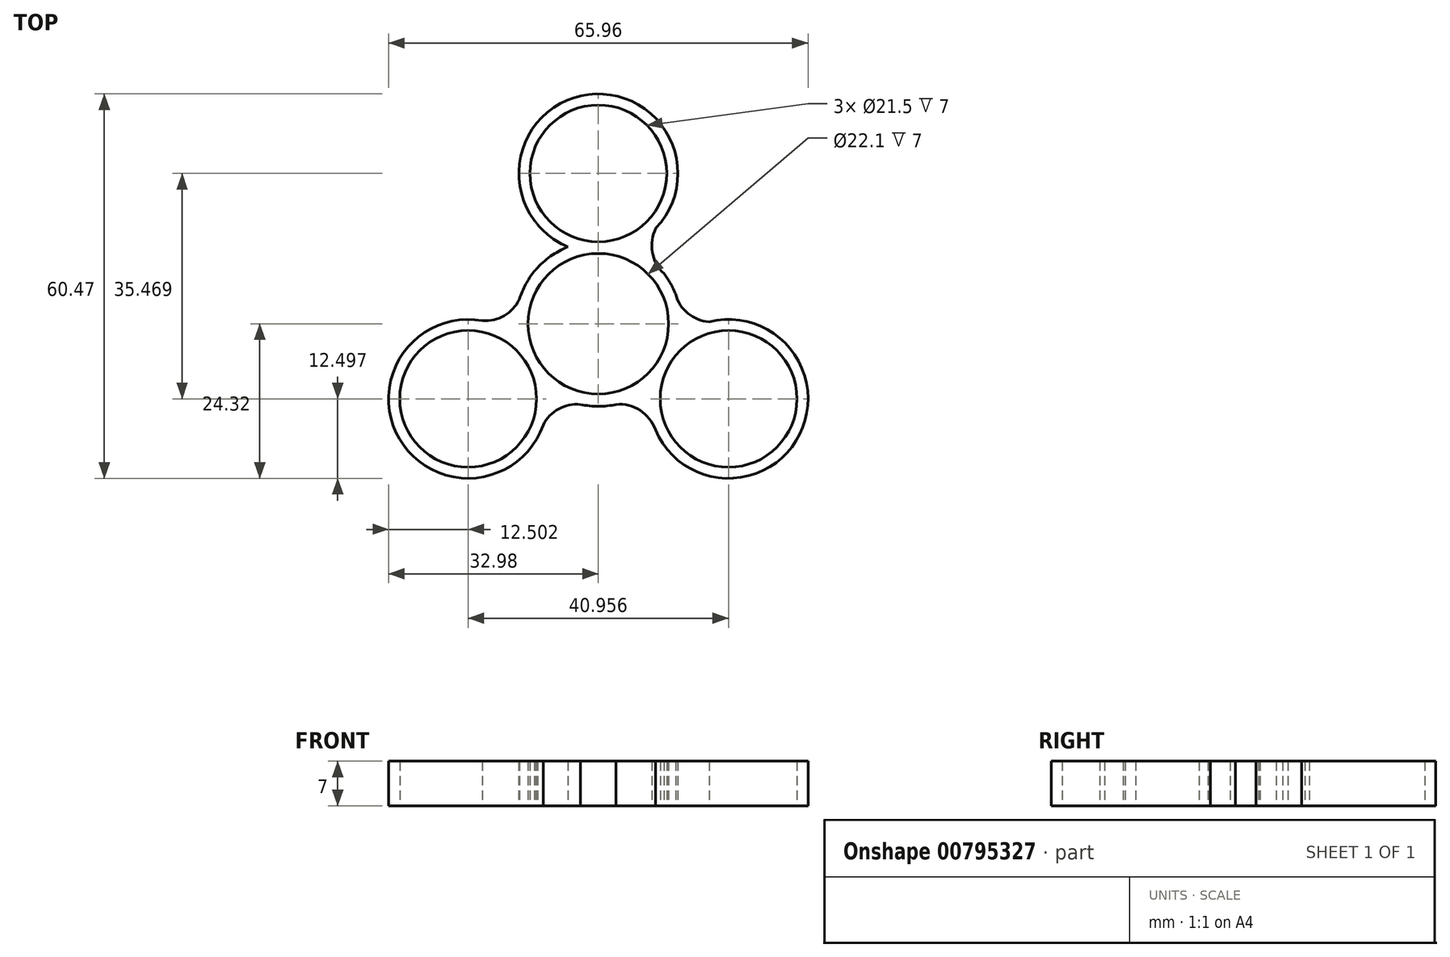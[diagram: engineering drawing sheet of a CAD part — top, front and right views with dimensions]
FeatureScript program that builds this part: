
annotation { "Feature Type Name" : "Feature", "Feature Type Description" : "" }
export const myFeature = defineFeature(function(context is Context, id is Id, definition is map)
    precondition{}
    {
        {
            var Q0;
            Q0=qCreatedBy(makeId("Top.planeOp"),FACE);
            var sketch = newSketch(context, id + "F0", { "sketchPlane" : qUnion([Q0])});
            skCircle(sketch, "E0", {"center": v(0, 0) * mm, "radius": 11.05 * mm});
            skCircle(sketch, "E1", {"center": v(0, 0) * mm, "radius": 13 * mm});
            skCircle(sketch, "E2", {"center": v(0, 23.65) * mm, "radius": 10.75 * mm});
            skCircle(sketch, "E3", {"center": v(0, 23.65) * mm, "radius": 12.5 * mm});
            skCircle(sketch, "E4", {"center": v(20.48, -11.82) * mm, "radius": 10.75 * mm});
            skCircle(sketch, "E5", {"center": v(20.48, -11.82) * mm, "radius": 12.5 * mm});
            skCircle(sketch, "E6", {"center": v(-20.48, -11.82) * mm, "radius": 10.75 * mm});
            skCircle(sketch, "E7", {"center": v(-20.48, -11.82) * mm, "radius": 12.5 * mm});
            skArc(sketch, "E8", {"start": v(-10.03, 8.27) * mm, "mid": v(-8.52, 12.26) * mm, "end": v(-10.07, 16.24) * mm});
            skArc(sketch, "E9", {"start": v(-19, 0.58) * mm, "mid": v(-14.79, 1.27) * mm, "end": v(-12.12, 4.6) * mm});
            skArc(sketch, "E10", {"start": v(9.9, 16.23) * mm, "mid": v(8.4, 11.97) * mm, "end": v(10.33, 7.9) * mm});
            skArc(sketch, "E11", {"start": v(12.14, 4.65) * mm, "mid": v(14.59, 1.27) * mm, "end": v(18.66, 0.33) * mm});
            skArc(sketch, "E12", {"start": v(9, -16.77) * mm, "mid": v(6.3, -13.46) * mm, "end": v(2.07, -12.8) * mm});
            skArc(sketch, "E13", {"start": v(-2.15, -12.8) * mm, "mid": v(-6.38, -13.49) * mm, "end": v(-9.04, -16.85) * mm});
            skSolve(sketch);
        }
        {
            var Q0;
            {var subQ1=sQuery(id+"F0.wireOp",EDGE,"E1");var subQ4=sQuery(id+"F0.wireOp",EDGE,"E7");var subQ7=makeQuery(id+"F0.imprint","INTERSECT",VERTEX,{"disambiguationData":[OD(0.0)],"derivedFrom":[subQ1,subQ4]});Q0=makeQuery(id+"F0.imprint","IMPRINT",FACE,{"disambiguationData":[TD([[makeQuery(id+"F0.imprint","IMPRINT",EDGE,{"disambiguationData":[TD([[subQ7,-1.0]])],"derivedFrom":subQ1}),-1.0]])]});}
            var Q1;
            {var subQ0=sQuery(id+"F0.wireOp",EDGE,"E9");var subQ1=sQuery(id+"F0.wireOp",EDGE,"E1");var subQ2=makeQuery(id+"F0.imprint","INTERSECT",VERTEX,{"derivedFrom":[subQ1,subQ0]});Q1=makeQuery(id+"F0.imprint","IMPRINT",FACE,{"disambiguationData":[TD([[makeQuery(id+"F0.imprint","IMPRINT",EDGE,{"disambiguationData":[TD([[subQ2,-1.0]])],"derivedFrom":subQ1}),-1.0]])]});}
            var Q2;
            Q2=makeQuery(id+"F0.imprint","IMPRINT",FACE,{"disambiguationData":[TD([[makeQuery(id+"F0.imprint","IMPRINT",EDGE,{"derivedFrom":sQuery(id+"F0.wireOp",EDGE,"E0")}),-1.0]])]});
            var Q3;
            {var subQ0=sQuery(id+"F0.wireOp",EDGE,"E7");var subQ1=sQuery(id+"F0.wireOp",EDGE,"E1");var subQ2=makeQuery(id+"F0.imprint","INTERSECT",VERTEX,{"disambiguationData":[OD(0.0)],"derivedFrom":[subQ1,subQ0]});Q3=makeQuery(id+"F0.imprint","IMPRINT",FACE,{"disambiguationData":[TD([[makeQuery(id+"F0.imprint","IMPRINT",EDGE,{"disambiguationData":[TD([[subQ2,-1.0]])],"derivedFrom":subQ1}),1.0]])]});}
            var Q4;
            {var subQ0=sQuery(id+"F0.wireOp",EDGE,"E12");var subQ1=sQuery(id+"F0.wireOp",EDGE,"E5");var subQ2=makeQuery(id+"F0.imprint","INTERSECT",VERTEX,{"disambiguationData":[OD(1.0)],"derivedFrom":[subQ1,subQ0]});Q4=makeQuery(id+"F0.imprint","IMPRINT",FACE,{"disambiguationData":[TD([[makeQuery(id+"F0.imprint","IMPRINT",EDGE,{"disambiguationData":[TD([[subQ2,1.0]])],"derivedFrom":subQ1}),-1.0]])]});}
            var Q5;
            {var subQ0=sQuery(id+"F0.wireOp",EDGE,"E13");var subQ1=sQuery(id+"F0.wireOp",EDGE,"E1");var subQ2=makeQuery(id+"F0.imprint","INTERSECT",VERTEX,{"derivedFrom":[subQ1,subQ0]});Q5=makeQuery(id+"F0.imprint","IMPRINT",FACE,{"disambiguationData":[TD([[makeQuery(id+"F0.imprint","IMPRINT",EDGE,{"disambiguationData":[TD([[subQ2,1.0]])],"derivedFrom":subQ1}),-1.0]])]});}
            var Q6;
            {var subQ3=sQuery(id+"F0.wireOp",EDGE,"E1");var subQ8=sQuery(id+"F0.wireOp",EDGE,"E4");var subQ9=makeQuery(id+"F0.imprint","INTERSECT",VERTEX,{"disambiguationData":[OD(0.0)],"derivedFrom":[subQ8,subQ3]});Q6=makeQuery(id+"F0.imprint","IMPRINT",FACE,{"disambiguationData":[TD([[makeQuery(id+"F0.imprint","IMPRINT",EDGE,{"disambiguationData":[TD([[subQ9,-1.0]])],"derivedFrom":subQ8}),-1.0]])]});}
            var Q7;
            {var subQ0=sQuery(id+"F0.wireOp",EDGE,"E1");var subQ1=sQuery(id+"F0.wireOp",EDGE,"E4");var subQ2=makeQuery(id+"F0.imprint","INTERSECT",VERTEX,{"disambiguationData":[OD(0.0)],"derivedFrom":[subQ1,subQ0]});Q7=makeQuery(id+"F0.imprint","IMPRINT",FACE,{"disambiguationData":[TD([[makeQuery(id+"F0.imprint","IMPRINT",EDGE,{"disambiguationData":[TD([[subQ2,1.0]])],"derivedFrom":subQ1}),-1.0]])]});}
            var Q8;
            {var subQ0=sQuery(id+"F0.wireOp",EDGE,"E11");var subQ1=sQuery(id+"F0.wireOp",EDGE,"E5");var subQ2=makeQuery(id+"F0.imprint","INTERSECT",VERTEX,{"derivedFrom":[subQ1,subQ0]});Q8=makeQuery(id+"F0.imprint","IMPRINT",FACE,{"disambiguationData":[TD([[makeQuery(id+"F0.imprint","IMPRINT",EDGE,{"disambiguationData":[TD([[subQ2,-1.0]])],"derivedFrom":subQ1}),-1.0]])]});}
            var Q9;
            {var subQ0=sQuery(id+"F0.wireOp",EDGE,"E1");var subQ1=sQuery(id+"F0.wireOp",EDGE,"E2");var subQ2=makeQuery(id+"F0.imprint","INTERSECT",VERTEX,{"disambiguationData":[OD(0.0)],"derivedFrom":[subQ1,subQ0]});Q9=makeQuery(id+"F0.imprint","IMPRINT",FACE,{"disambiguationData":[TD([[makeQuery(id+"F0.imprint","IMPRINT",EDGE,{"disambiguationData":[TD([[subQ2,1.0]])],"derivedFrom":subQ1}),-1.0]])]});}
            var Q10;
            {var subQ0=sQuery(id+"F0.wireOp",EDGE,"E10");var subQ1=sQuery(id+"F0.wireOp",EDGE,"E3");var subQ2=makeQuery(id+"F0.imprint","INTERSECT",VERTEX,{"derivedFrom":[subQ1,subQ0]});Q10=makeQuery(id+"F0.imprint","IMPRINT",FACE,{"disambiguationData":[TD([[makeQuery(id+"F0.imprint","IMPRINT",EDGE,{"disambiguationData":[TD([[subQ2,1.0]])],"derivedFrom":subQ1}),-1.0]])]});}
            var Q11;
            {var subQ2=sQuery(id+"F0.wireOp",EDGE,"E1");var subQ8=sQuery(id+"F0.wireOp",EDGE,"E2");var subQ9=makeQuery(id+"F0.imprint","INTERSECT",VERTEX,{"disambiguationData":[OD(0.0)],"derivedFrom":[subQ8,subQ2]});Q11=makeQuery(id+"F0.imprint","IMPRINT",FACE,{"disambiguationData":[TD([[makeQuery(id+"F0.imprint","IMPRINT",EDGE,{"disambiguationData":[TD([[subQ9,-1.0]])],"derivedFrom":subQ8}),-1.0]])]});}
            var Q12;
            {var subQ0=sQuery(id+"F0.wireOp",EDGE,"E8");var subQ1=sQuery(id+"F0.wireOp",EDGE,"E3");var subQ2=makeQuery(id+"F0.imprint","INTERSECT",VERTEX,{"disambiguationData":[OD(1.0)],"derivedFrom":[subQ1,subQ0]});Q12=makeQuery(id+"F0.imprint","IMPRINT",FACE,{"disambiguationData":[TD([[makeQuery(id+"F0.imprint","IMPRINT",EDGE,{"disambiguationData":[TD([[subQ2,-1.0]])],"derivedFrom":subQ1}),-1.0]])]});}
            extrude(context, id + "F1", {"entities" : qUnion([Q0, Q1, Q2, Q3, Q4, Q5, Q6, Q7, Q8, Q9, Q10, Q11, Q12]), "depth" : 7 * mm, "offsetDistance" : 25 * mm});
        }
    });
